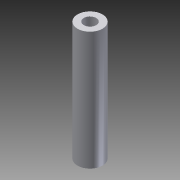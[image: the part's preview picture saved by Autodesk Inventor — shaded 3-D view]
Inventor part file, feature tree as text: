
AUTODESK INVENTOR PART (.ipt)
format: ipt  version: 2015 (Build 190159000, 159)  size: 71,680 bytes
history: native  units: mm
features: extrude x1
ambient origin geometry x8: Origin, YZ Plane, XZ Plane, XY Plane, X Axis, Y Axis, Z Axis, Center Point
bodies: Solid1 (feature_tree)
feature tree (1):
  extrude  "Extrusión1"  Depth=2.0mm
